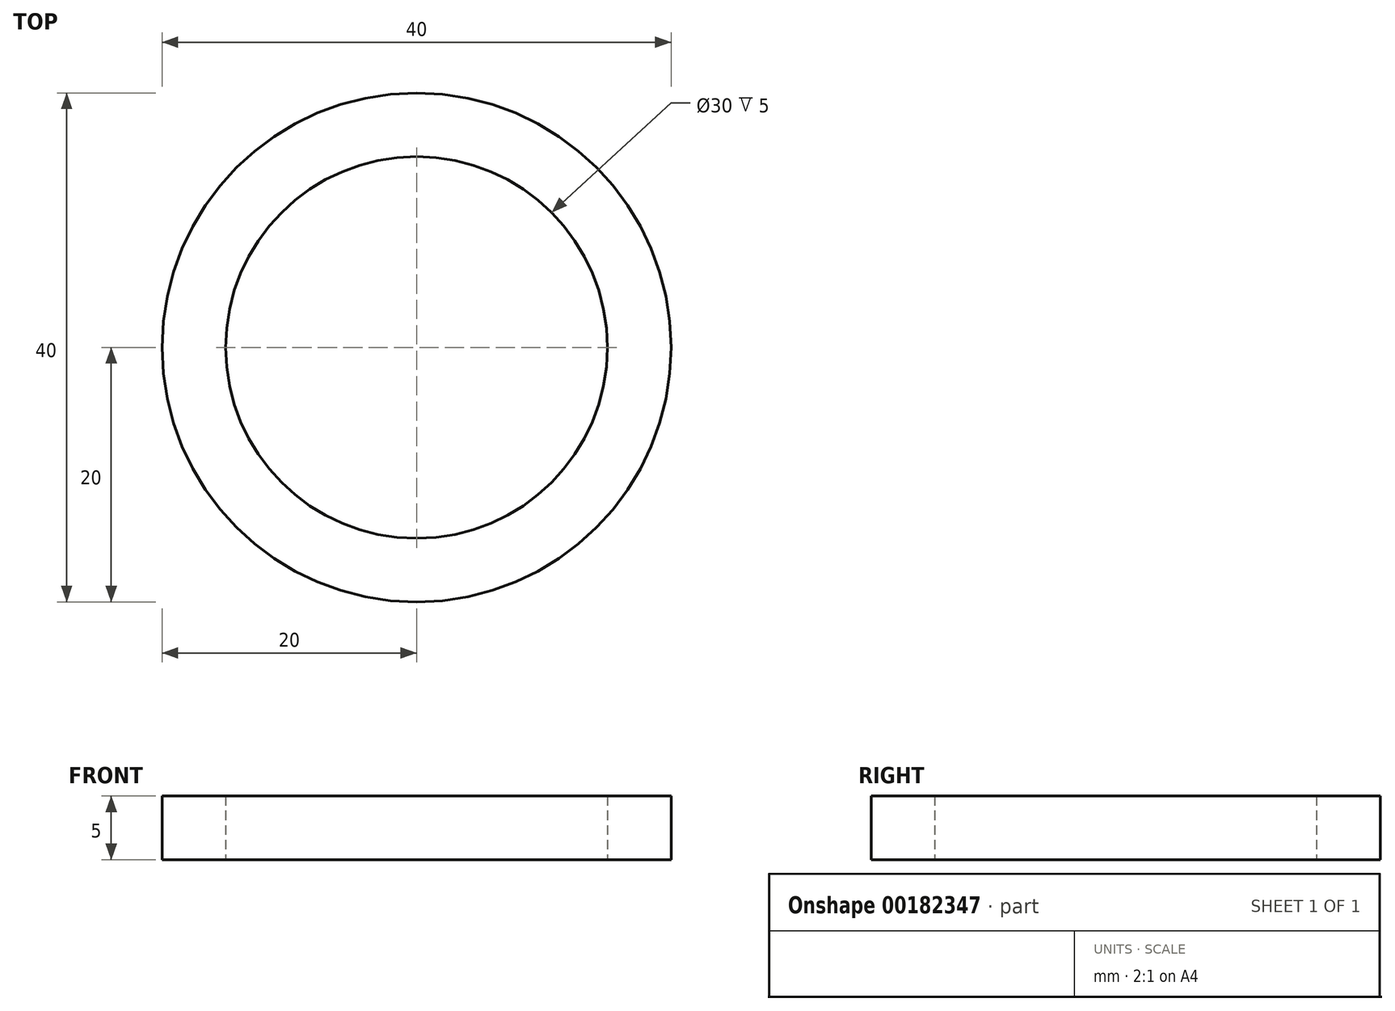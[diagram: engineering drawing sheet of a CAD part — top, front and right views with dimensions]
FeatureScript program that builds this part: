
annotation { "Feature Type Name" : "Feature", "Feature Type Description" : "" }
export const myFeature = defineFeature(function(context is Context, id is Id, definition is map)
    precondition{}
    {
        {
            var Q0;
            Q0=qCreatedBy(makeId("Top.planeOp"),FACE);
            var sketch = newSketch(context, id + "F0", { "sketchPlane" : qUnion([Q0])});
            skCircle(sketch, "E0", {"center": v(0, 0) * mm, "radius": 20 * mm});
            skCircle(sketch, "E1", {"center": v(0, 0) * mm, "radius": 15 * mm});
            skSolve(sketch);
        }
        {
            var Q0;
            Q0 = qSketchRegion(id + "F0", true);
            extrude(context, id + "F1", {"entities" : qUnion([Q0]), "depth" : 5 * mm});
        }
    });
